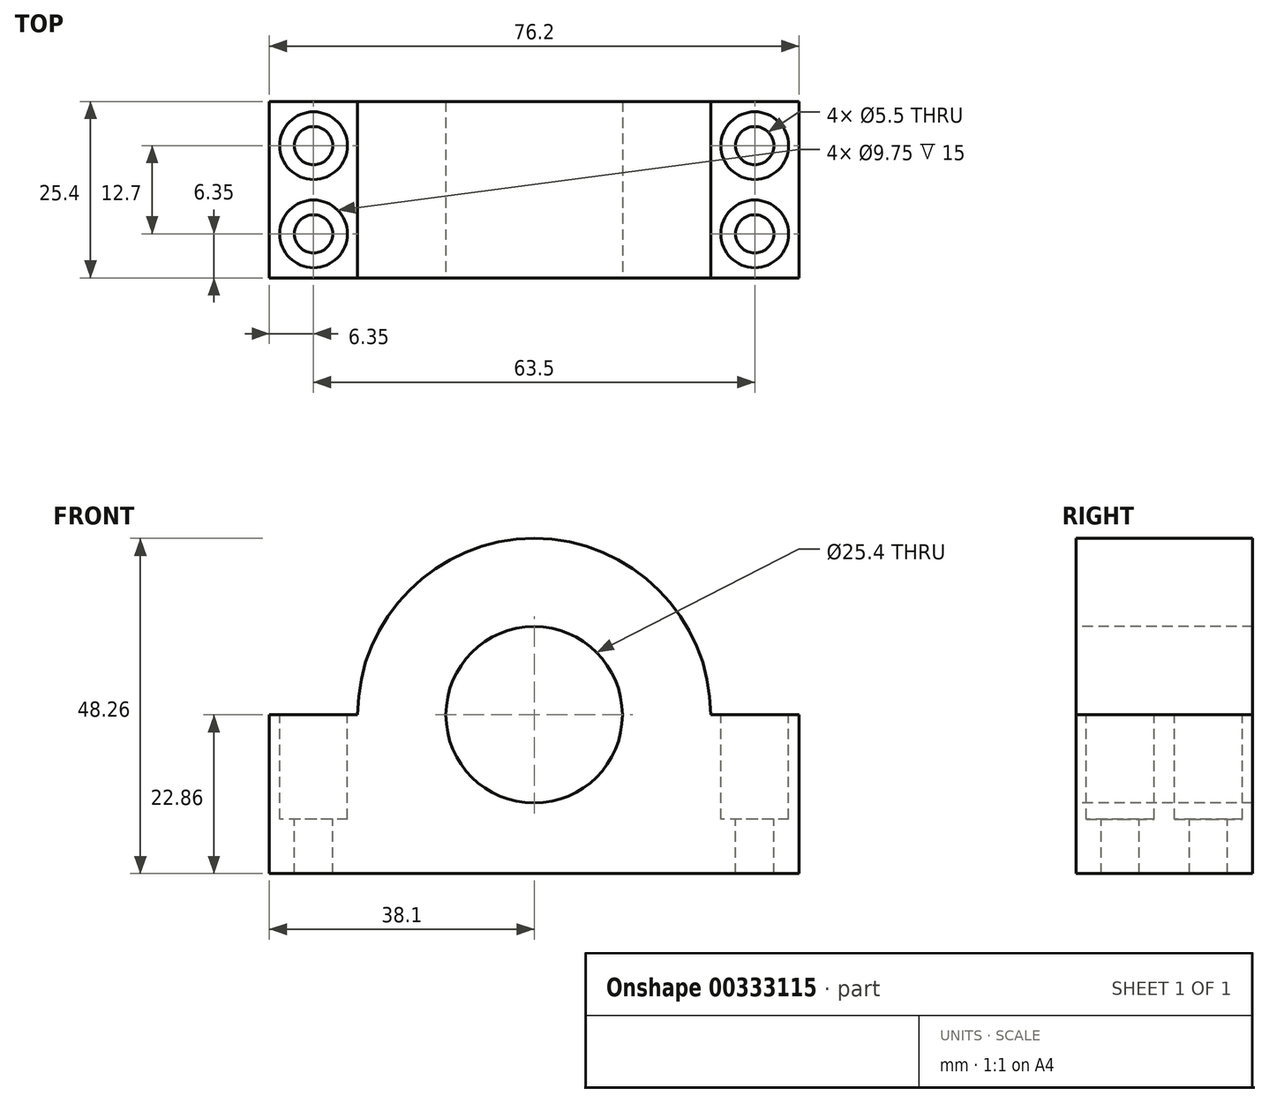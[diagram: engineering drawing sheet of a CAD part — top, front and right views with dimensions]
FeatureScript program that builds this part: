
annotation { "Feature Type Name" : "Feature", "Feature Type Description" : "" }
export const myFeature = defineFeature(function(context is Context, id is Id, definition is map)
    precondition{}
    {
        {
            var Q0;
            Q0=qCreatedBy(makeId("Front.planeOp"),FACE);
            var sketch = newSketch(context, id + "F0", { "sketchPlane" : qUnion([Q0])});
            skLineSegment(sketch, "E0.bottom", {"start": v(38.1, 25.4) * mm, "end": v(-38.1, 25.4) * mm});
            skLineSegment(sketch, "E0.top", {"start": v(38.1, -25.4) * mm, "end": v(-38.1, -25.4) * mm});
            skLineSegment(sketch, "E0.left", {"start": v(38.1, 25.4) * mm, "end": v(38.1, -25.4) * mm});
            skLineSegment(sketch, "E0.right", {"start": v(-38.1, 25.4) * mm, "end": v(-38.1, -25.4) * mm});
            skPoint(sketch, "E0.middle", {"position": v(0, 0) * mm});
            skSolve(sketch);
        }
        {
            var Q0;
            Q0=qSketchRegion(id+"F0",true);
            extrude(context, id + "F1", {"entities" : qUnion([Q0]), "depth" : 25.4 * mm});
        }
        {
            var Q0;
            Q0=makeQuery(id+"F1.opExtrude","CAP_FACE",FACE,{"disambiguationData":[OSD([sQuery(id+"F0.wireOp",EDGE,"E0.bottom"),sQuery(id+"F0.wireOp",EDGE,"E0.top"),sQuery(id+"F0.wireOp",EDGE,"E0.left"),sQuery(id+"F0.wireOp",EDGE,"E0.right")])],"isStart":false});
            var sketch = newSketch(context, id + "F2", { "sketchPlane" : qUnion([Q0])});
            skCircle(sketch, "E1", {"center": v(0, 0) * mm, "radius": 12.7 * mm});
            skSolve(sketch);
        }
        {
            var Q0;
            Q0=qSketchRegion(id+"F2",true);
            extrude(context, id + "F3", {"entities" : qUnion([Q0]), "operationType" : NewBodyOperationType.REMOVE, "oppositeDirection" : true, "depth" : 32.77 * mm});
        }
        {
            var Q0;
            Q0=makeQuery(id+"F1.opExtrude","CAP_FACE",FACE,{"disambiguationData":[OSD([sQuery(id+"F0.wireOp",EDGE,"E0.bottom"),sQuery(id+"F0.wireOp",EDGE,"E0.top"),sQuery(id+"F0.wireOp",EDGE,"E0.left"),sQuery(id+"F0.wireOp",EDGE,"E0.right")])],"isStart":false});
            var sketch = newSketch(context, id + "F4", { "sketchPlane" : qUnion([Q0])});
            skCircle(sketch, "E2.0", {"center": v(0, 0) * mm, "radius": 12.7 * mm});
            skCircle(sketch, "E3", {"center": v(0, 0) * mm, "radius": 25.4 * mm});
            skLineSegment(sketch, "E4", {"start": v(-38.1, 0) * mm, "end": v(-25.4, 0) * mm});
            skLineSegment(sketch, "E5", {"start": v(0, 0) * mm, "end": v(0, 25.4) * mm, "construction": true});
            skLineSegment(sketch, "E6.MirrorCS", {"start": v(38.1, 0) * mm, "end": v(25.4, 0) * mm});
            skSolve(sketch);
        }
        {
            var Q0;
            {var subQ0=sQuery(id+"F4.wireOp",EDGE,"E6.MirrorCS");Q0=makeQuery(id+"F4.imprint","IMPRINT",FACE,{"disambiguationData":[TD([[makeQuery(id+"F4.imprint","IMPRINT",EDGE,{"derivedFrom":subQ0}),-1.0]])]});}
            var Q1;
            {var subQ0=sQuery(id+"F4.wireOp",EDGE,"E4");Q1=makeQuery(id+"F4.imprint","IMPRINT",FACE,{"disambiguationData":[TD([[makeQuery(id+"F4.imprint","IMPRINT",EDGE,{"derivedFrom":subQ0}),1.0]])]});}
            extrude(context, id + "F5", {"entities" : qUnion([Q0, Q1]), "operationType" : NewBodyOperationType.REMOVE, "oppositeDirection" : true, "depth" : 25.4 * mm});
        }
        {
            var Q0;
            Q0=makeQuery(id+"F5.boolean.opBoolean","COPY",FACE,{"derivedFrom":makeQuery(id+"F5.opExtrude","SWEPT_FACE",FACE,{"disambiguationData":[OSD([sQuery(id+"F4.wireOp",EDGE,"E4")])]})});
            var sketch = newSketch(context, id + "F6", { "sketchPlane" : qUnion([Q0])});
            skPoint(sketch, "E7", {"position": v(-31.75, -6.35) * mm});
            skPoint(sketch, "E8", {"position": v(-31.75, -19.05) * mm});
            skPoint(sketch, "E9", {"position": v(31.75, -6.35) * mm});
            skPoint(sketch, "E10", {"position": v(31.75, -19.05) * mm});
            skLineSegment(sketch, "E11", {"start": v(0, 0) * mm, "end": v(0, -4.28) * mm, "construction": true});
            skLineSegment(sketch, "E12", {"start": v(-38.1, -12.7) * mm, "end": v(-31.32, -12.7) * mm, "construction": true});
            skLineSegment(sketch, "E13", {"start": v(31.75, -25.4) * mm, "end": v(31.75, -22.7) * mm, "construction": true});
            skLineSegment(sketch, "E14", {"start": v(-38.1, -12.7) * mm, "end": v(-38.1, 0) * mm, "construction": true});
            skLineSegment(sketch, "E15", {"start": v(-38.1, 0) * mm, "end": v(-38.1, -6.35) * mm, "construction": true});
            skLineSegment(sketch, "E16", {"start": v(-38.1, -6.35) * mm, "end": v(-35.3, -6.35) * mm, "construction": true});
            skSolve(sketch);
        }
        {
            var Q0;
            Q0=sQuery(id+"F6.wireOp",VERTEX,"E7");
            var Q1;
            Q1=sQuery(id+"F6.wireOp",VERTEX,"E8");
            var Q2;
            Q2=sQuery(id+"F6.wireOp",VERTEX,"E9");
            var Q3;
            Q3=sQuery(id+"F6.wireOp",VERTEX,"E10");
            var Q4;
            Q4=makeQuery(id+"F1.opExtrude","SWEPT_BODY",BODY,{"disambiguationData":[OSD([sQuery(id+"F0.wireOp",EDGE,"E0.bottom"),sQuery(id+"F0.wireOp",EDGE,"E0.top"),sQuery(id+"F0.wireOp",EDGE,"E0.left"),sQuery(id+"F0.wireOp",EDGE,"E0.right")])]});
            hole(context, id + "F7", {"style" : HoleStyle.C_BORE, "endStyle" : HoleEndStyle.BLIND, "holeDiameter" : 5.5 * mm, "cBoreDiameter" : 9.75 * mm, "cBoreDepth" : 15 * mm, "holeDepth" : 254 * mm, "tappedDepth" : 12.7 * mm, "tapClearance" : 3, "locations" : qUnion([Q0, Q1, Q2, Q3]), "scope" : qUnion([Q4])});
        }
        {
            var Q0;
            Q0=makeQuery(id+"F1.opExtrude","SWEPT_FACE",FACE,{"disambiguationData":[OSD([sQuery(id+"F0.wireOp",EDGE,"E0.top")])]});
            extrude(context, id + "F8", {"entities" : qUnion([Q0]), "operationType" : NewBodyOperationType.REMOVE, "oppositeDirection" : true, "depth" : 2.54 * mm});
        }
    });
